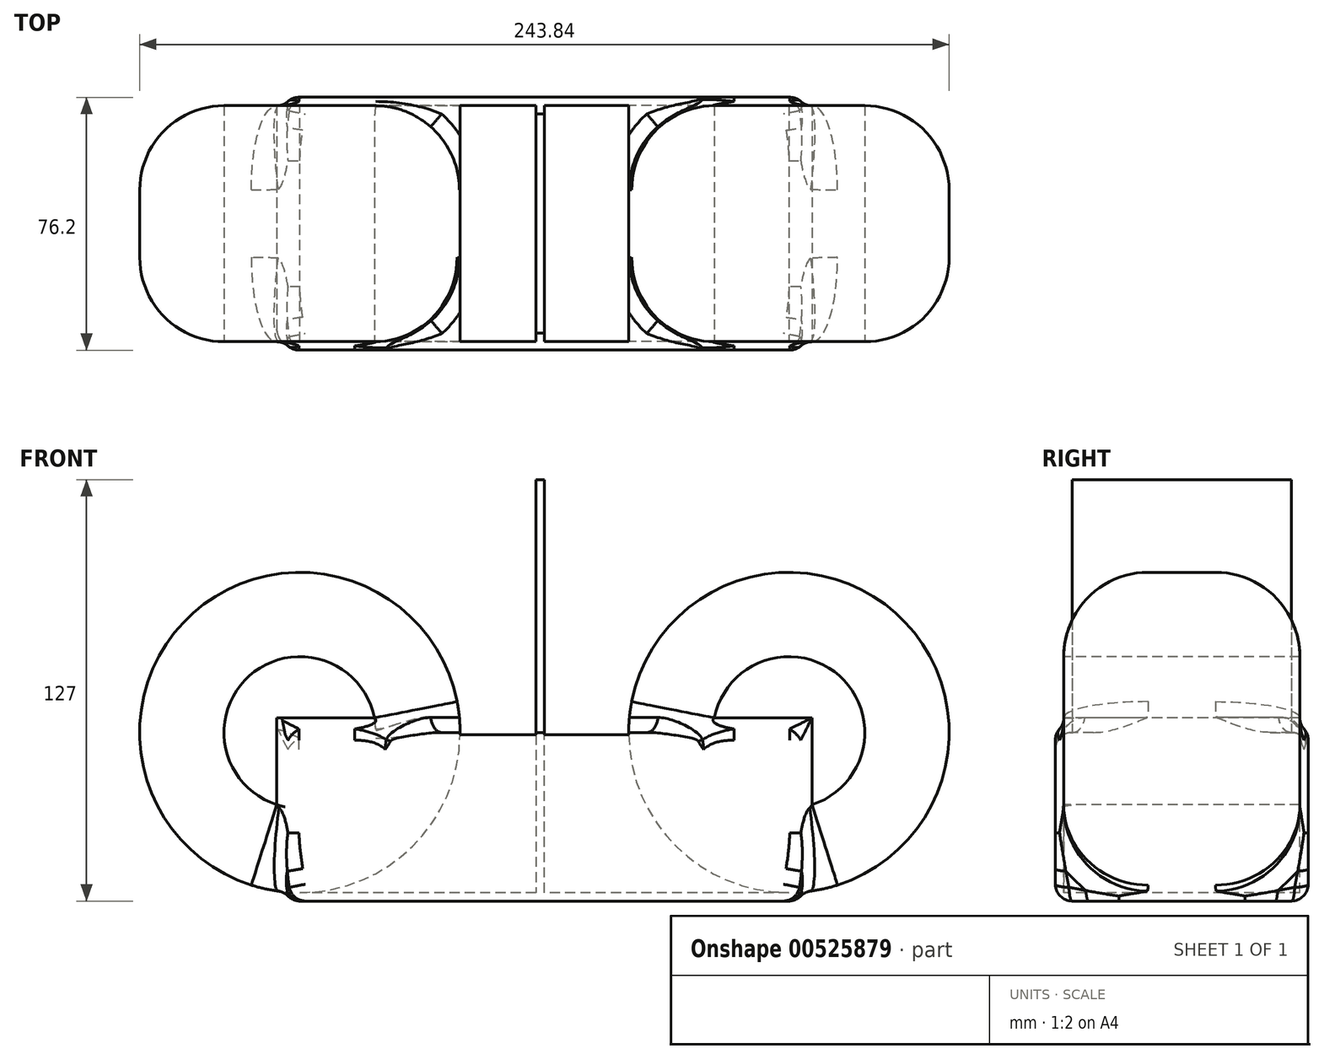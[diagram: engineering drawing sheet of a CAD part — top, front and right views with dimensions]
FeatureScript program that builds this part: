
annotation { "Feature Type Name" : "Feature", "Feature Type Description" : "" }
export const myFeature = defineFeature(function(context is Context, id is Id, definition is map)
    precondition{}
    {
        {
            var Q0;
            Q0=qCreatedBy(makeId("Top.planeOp"),FACE);
            var sketch = newSketch(context, id + "F0", { "sketchPlane" : qUnion([Q0])});
            skLineSegment(sketch, "E0.bottom", {"start": v(0, -43.56) * mm, "end": v(-76.2, -43.56) * mm});
            skLineSegment(sketch, "E0.top", {"start": v(0, 32.64) * mm, "end": v(-76.2, 32.64) * mm});
            skLineSegment(sketch, "E0.left", {"start": v(0, -43.56) * mm, "end": v(0, 32.64) * mm});
            skLineSegment(sketch, "E0.right", {"start": v(-76.2, -43.56) * mm, "end": v(-76.2, 32.64) * mm});
            skLineSegment(sketch, "E1.bottom", {"start": v(0, 32.64) * mm, "end": v(76.2, 32.64) * mm});
            skLineSegment(sketch, "E1.top", {"start": v(0, -43.56) * mm, "end": v(76.2, -43.56) * mm});
            skLineSegment(sketch, "E1.left", {"start": v(0, 32.64) * mm, "end": v(0, -43.56) * mm});
            skLineSegment(sketch, "E1.right", {"start": v(76.2, 32.64) * mm, "end": v(76.2, -43.56) * mm});
            skSolve(sketch);
        }
        {
            var Q0;
            Q0=makeQuery(id+"F0.imprint","IMPRINT",FACE,{"disambiguationData":[TD([[makeQuery(id+"F0.imprint","IMPRINT",EDGE,{"derivedFrom":sQuery(id+"F0.wireOp",EDGE,"E0.bottom")}),-1.0]])]});
            extrude(context, id + "F1", {"entities" : qUnion([Q0]), "depth" : 25.4 * mm, "offsetDistance" : 25.4 * mm});
        }
        {
            var Q0;
            Q0=makeQuery(id+"F1.opExtrude","CAP_FACE",FACE,{"disambiguationData":[OSD([sQuery(id+"F0.wireOp",EDGE,"E0.bottom"),sQuery(id+"F0.wireOp",EDGE,"E0.top"),sQuery(id+"F0.wireOp",EDGE,"E0.right"),sQuery(id+"F0.wireOp",EDGE,"E1.left")])],"isStart":false});
            shell(context, id + "F2", {"entities" : qUnion([Q0]), "thickness" : 2.54 * mm});
        }
        {
            var Q0;
            Q0=makeQuery(id+"F0.imprint","IMPRINT",FACE,{"disambiguationData":[TD([[makeQuery(id+"F0.imprint","IMPRINT",EDGE,{"derivedFrom":sQuery(id+"F0.wireOp",EDGE,"E1.bottom")}),-1.0]])]});
            extrude(context, id + "F3", {"entities" : qUnion([Q0]), "operationType" : NewBodyOperationType.ADD, "depth" : 25.4 * mm, "offsetDistance" : 25.4 * mm});
        }
        {
            var Q0;
            {var subQ0=sQuery(id+"F0.wireOp",EDGE,"E1.left");Q0=makeQuery(id+"F3.boolean.opBoolean","MERGE",FACE,{"derivedFrom":[makeQuery(id+"F1.opExtrude","CAP_FACE",FACE,{"disambiguationData":[OSD([sQuery(id+"F0.wireOp",EDGE,"E0.bottom"),sQuery(id+"F0.wireOp",EDGE,"E0.top"),sQuery(id+"F0.wireOp",EDGE,"E0.right"),subQ0])],"isStart":false}),makeQuery(id+"F3.opExtrude","CAP_FACE",FACE,{"disambiguationData":[OSD([sQuery(id+"F0.wireOp",EDGE,"E1.bottom"),sQuery(id+"F0.wireOp",EDGE,"E1.top"),subQ0,sQuery(id+"F0.wireOp",EDGE,"E1.right")])],"isStart":false})]});}
            shell(context, id + "F4", {"entities" : qUnion([Q0]), "thickness" : 2.54 * mm});
        }
        {
            var Q0;
            {var subQ0=sQuery(id+"F0.wireOp",EDGE,"E1.left");Q0=makeQuery(id+"F3.boolean.opBoolean","MERGE",FACE,{"derivedFrom":[makeQuery(id+"F1.opExtrude","CAP_FACE",FACE,{"disambiguationData":[OSD([sQuery(id+"F0.wireOp",EDGE,"E0.bottom"),sQuery(id+"F0.wireOp",EDGE,"E0.top"),sQuery(id+"F0.wireOp",EDGE,"E0.right"),subQ0])],"isStart":false}),makeQuery(id+"F3.opExtrude","CAP_FACE",FACE,{"disambiguationData":[OSD([sQuery(id+"F0.wireOp",EDGE,"E1.bottom"),sQuery(id+"F0.wireOp",EDGE,"E1.top"),subQ0,sQuery(id+"F0.wireOp",EDGE,"E1.right")])],"isStart":false})]});}
            extrude(context, id + "F5", {"entities" : qUnion([Q0]), "operationType" : NewBodyOperationType.ADD, "depth" : 25.4 * mm, "offsetDistance" : 25.4 * mm});
        }
        {
            var Q0;
            {var subQ0=sQuery(id+"F0.wireOp",EDGE,"E0.right");Q0=makeQuery(id+"F5.boolean.opBoolean","MERGE",FACE,{"derivedFrom":[makeQuery(id+"F2.opShell","OFFSET_FACE",FACE,{"disambiguationData":[OSD([subQ0])]}),makeQuery(id+"F5.opExtrude","SWEPT_FACE",FACE,{"disambiguationData":[OSD([subQ0]),TDD([makeQuery(id+"F2.opShell","OFFSET_EDGE",EDGE,{"disambiguationData":[OSD([subQ0]),TDD([makeQuery(id+"F1.opExtrude","CAP_EDGE",EDGE,{"disambiguationData":[OSD([subQ0])],"isStart":false})])]})])]})]});}
            var Q1;
            {var subQ0=sQuery(id+"F0.wireOp",EDGE,"E0.right");Q1=makeQuery(id+"F5.opExtrude","CAP_EDGE",EDGE,{"disambiguationData":[OSD([subQ0]),TDD([makeQuery(id+"F2.opShell","OFFSET_EDGE",EDGE,{"disambiguationData":[OSD([subQ0]),TDD([makeQuery(id+"F1.opExtrude","CAP_EDGE",EDGE,{"disambiguationData":[OSD([subQ0])],"isStart":false})])]})])],"isStart":false});}
            revolve(context, id + "F6", {"operationType" : NewBodyOperationType.ADD, "entities" : qUnion([Q0]), "axis" : qUnion([Q1]), "revolveType" : RevolveType.FULL});
        }
        {
            var Q0;
            {var subQ0=sQuery(id+"F0.wireOp",EDGE,"E1.right");Q0=makeQuery(id+"F5.boolean.opBoolean","MERGE",FACE,{"derivedFrom":[makeQuery(id+"F4.opShell","OFFSET_FACE",FACE,{"disambiguationData":[OSD([subQ0])]}),makeQuery(id+"F5.opExtrude","SWEPT_FACE",FACE,{"disambiguationData":[OSD([subQ0]),TDD([makeQuery(id+"F4.opShell","OFFSET_EDGE",EDGE,{"disambiguationData":[OSD([subQ0]),TDD([makeQuery(id+"F3.opExtrude","CAP_EDGE",EDGE,{"disambiguationData":[OSD([subQ0])],"isStart":false})])]})])]})]});}
            var Q1;
            {var subQ0=sQuery(id+"F0.wireOp",EDGE,"E1.right");Q1=makeQuery(id+"F5.opExtrude","CAP_EDGE",EDGE,{"disambiguationData":[OSD([subQ0]),TDD([makeQuery(id+"F4.opShell","OFFSET_EDGE",EDGE,{"disambiguationData":[OSD([subQ0]),TDD([makeQuery(id+"F3.opExtrude","CAP_EDGE",EDGE,{"disambiguationData":[OSD([subQ0])],"isStart":false})])]})])],"isStart":false});}
            revolve(context, id + "F7", {"operationType" : NewBodyOperationType.ADD, "entities" : qUnion([Q0]), "axis" : qUnion([Q1]), "revolveType" : RevolveType.FULL});
        }
        {
            var Q0;
            {var subQ0=sQuery(id+"F0.wireOp",EDGE,"E0.right");var subQ1=sQuery(id+"F0.wireOp",EDGE,"E0.bottom");Q0=makeQuery(id+"F6.boolean.opBoolean","INTERSECT",EDGE,{"derivedFrom":[makeQuery(id+"F5.opExtrude","CAP_FACE",FACE,{"disambiguationData":[OSD([subQ1,sQuery(id+"F0.wireOp",EDGE,"E0.top"),subQ0,sQuery(id+"F0.wireOp",EDGE,"E1.bottom"),sQuery(id+"F0.wireOp",EDGE,"E1.top"),sQuery(id+"F0.wireOp",EDGE,"E1.left"),sQuery(id+"F0.wireOp",EDGE,"E1.right")])],"isStart":false}),makeQuery(id+"F6.opRevolve","SWEPT_FACE",FACE,{"disambiguationData":[OSD([subQ1,subQ0])]})]});}
            var Q1;
            {var subQ0=sQuery(id+"F0.wireOp",EDGE,"E0.right");Q1=makeQuery(id+"F6.boolean.opBoolean","INTERSECT",EDGE,{"derivedFrom":[makeQuery(id+"F5.boolean.opBoolean","MERGE",FACE,{"derivedFrom":[makeQuery(id+"F1.opExtrude","SWEPT_FACE",FACE,{"disambiguationData":[OSD([subQ0])]}),makeQuery(id+"F5.opExtrude","SWEPT_FACE",FACE,{"disambiguationData":[OSD([subQ0]),TDD([makeQuery(id+"F1.opExtrude","CAP_EDGE",EDGE,{"disambiguationData":[OSD([subQ0])],"isStart":false})])]})]}),makeQuery(id+"F6.opRevolve","SWEPT_FACE",FACE,{"disambiguationData":[OSD([sQuery(id+"F0.wireOp",EDGE,"E0.bottom"),subQ0])]})]});}
            var Q2;
            {var subQ0=sQuery(id+"F0.wireOp",EDGE,"E0.right");Q2=makeQuery(id+"F6.boolean.opBoolean","INTERSECT",EDGE,{"derivedFrom":[makeQuery(id+"F5.boolean.opBoolean","MERGE",FACE,{"derivedFrom":[makeQuery(id+"F1.opExtrude","SWEPT_FACE",FACE,{"disambiguationData":[OSD([subQ0])]}),makeQuery(id+"F5.opExtrude","SWEPT_FACE",FACE,{"disambiguationData":[OSD([subQ0]),TDD([makeQuery(id+"F1.opExtrude","CAP_EDGE",EDGE,{"disambiguationData":[OSD([subQ0])],"isStart":false})])]})]}),makeQuery(id+"F6.opRevolve","SWEPT_FACE",FACE,{"disambiguationData":[OSD([subQ0])]})]});}
            var Q3;
            {var subQ0=sQuery(id+"F0.wireOp",EDGE,"E0.right");Q3=makeQuery(id+"F6.boolean.opBoolean","INTERSECT",EDGE,{"derivedFrom":[makeQuery(id+"F5.boolean.opBoolean","MERGE",FACE,{"derivedFrom":[makeQuery(id+"F1.opExtrude","SWEPT_FACE",FACE,{"disambiguationData":[OSD([subQ0])]}),makeQuery(id+"F5.opExtrude","SWEPT_FACE",FACE,{"disambiguationData":[OSD([subQ0]),TDD([makeQuery(id+"F1.opExtrude","CAP_EDGE",EDGE,{"disambiguationData":[OSD([subQ0])],"isStart":false})])]})]}),makeQuery(id+"F6.opRevolve","SWEPT_FACE",FACE,{"disambiguationData":[OSD([sQuery(id+"F0.wireOp",EDGE,"E0.top"),subQ0])]})]});}
            var Q4;
            {var subQ0=sQuery(id+"F0.wireOp",EDGE,"E1.right");Q4=makeQuery(id+"F7.boolean.opBoolean","INTERSECT",EDGE,{"derivedFrom":[makeQuery(id+"F5.boolean.opBoolean","MERGE",FACE,{"derivedFrom":[makeQuery(id+"F3.opExtrude","SWEPT_FACE",FACE,{"disambiguationData":[OSD([subQ0])]}),makeQuery(id+"F5.opExtrude","SWEPT_FACE",FACE,{"disambiguationData":[OSD([subQ0]),TDD([makeQuery(id+"F3.opExtrude","CAP_EDGE",EDGE,{"disambiguationData":[OSD([subQ0])],"isStart":false})])]})]}),makeQuery(id+"F7.opRevolve","SWEPT_FACE",FACE,{"disambiguationData":[OSD([sQuery(id+"F0.wireOp",EDGE,"E1.bottom"),subQ0])]})]});}
            var Q5;
            {var subQ0=sQuery(id+"F0.wireOp",EDGE,"E1.right");var subQ1=sQuery(id+"F0.wireOp",EDGE,"E1.bottom");Q5=makeQuery(id+"F7.boolean.opBoolean","INTERSECT",EDGE,{"derivedFrom":[makeQuery(id+"F5.opExtrude","CAP_FACE",FACE,{"disambiguationData":[OSD([sQuery(id+"F0.wireOp",EDGE,"E0.bottom"),sQuery(id+"F0.wireOp",EDGE,"E0.top"),sQuery(id+"F0.wireOp",EDGE,"E0.right"),subQ1,sQuery(id+"F0.wireOp",EDGE,"E1.top"),sQuery(id+"F0.wireOp",EDGE,"E1.left"),subQ0])],"isStart":false}),makeQuery(id+"F7.opRevolve","SWEPT_FACE",FACE,{"disambiguationData":[OSD([subQ1,subQ0])]})]});}
            var Q6;
            {var subQ0=sQuery(id+"F0.wireOp",EDGE,"E1.right");Q6=makeQuery(id+"F7.boolean.opBoolean","INTERSECT",EDGE,{"derivedFrom":[makeQuery(id+"F5.boolean.opBoolean","MERGE",FACE,{"derivedFrom":[makeQuery(id+"F3.opExtrude","SWEPT_FACE",FACE,{"disambiguationData":[OSD([subQ0])]}),makeQuery(id+"F5.opExtrude","SWEPT_FACE",FACE,{"disambiguationData":[OSD([subQ0]),TDD([makeQuery(id+"F3.opExtrude","CAP_EDGE",EDGE,{"disambiguationData":[OSD([subQ0])],"isStart":false})])]})]}),makeQuery(id+"F7.opRevolve","SWEPT_FACE",FACE,{"disambiguationData":[OSD([sQuery(id+"F0.wireOp",EDGE,"E1.top"),subQ0])]})]});}
            var Q7;
            {var subQ0=sQuery(id+"F0.wireOp",EDGE,"E1.right");Q7=makeQuery(id+"F7.boolean.opBoolean","INTERSECT",EDGE,{"derivedFrom":[makeQuery(id+"F5.boolean.opBoolean","MERGE",FACE,{"derivedFrom":[makeQuery(id+"F3.opExtrude","SWEPT_FACE",FACE,{"disambiguationData":[OSD([subQ0])]}),makeQuery(id+"F5.opExtrude","SWEPT_FACE",FACE,{"disambiguationData":[OSD([subQ0]),TDD([makeQuery(id+"F3.opExtrude","CAP_EDGE",EDGE,{"disambiguationData":[OSD([subQ0])],"isStart":false})])]})]}),makeQuery(id+"F7.opRevolve","SWEPT_FACE",FACE,{"disambiguationData":[OSD([subQ0])]})]});}
            var Q8;
            {var subQ0=sQuery(id+"F0.wireOp",EDGE,"E1.right");var subQ1=sQuery(id+"F0.wireOp",EDGE,"E1.top");Q8=makeQuery(id+"F7.boolean.opBoolean","INTERSECT",EDGE,{"derivedFrom":[makeQuery(id+"F5.opExtrude","CAP_FACE",FACE,{"disambiguationData":[OSD([sQuery(id+"F0.wireOp",EDGE,"E0.bottom"),sQuery(id+"F0.wireOp",EDGE,"E0.top"),sQuery(id+"F0.wireOp",EDGE,"E0.right"),sQuery(id+"F0.wireOp",EDGE,"E1.bottom"),subQ1,sQuery(id+"F0.wireOp",EDGE,"E1.left"),subQ0])],"isStart":false}),makeQuery(id+"F7.opRevolve","SWEPT_FACE",FACE,{"disambiguationData":[OSD([subQ1,subQ0])]})]});}
            fillet(context, id + "F8", {"entities" : qUnion([Q0, Q1, Q2, Q3, Q4, Q5, Q6, Q7, Q8]), "radius" : 5.08 * mm, "tangentPropagation" : true, "allowEdgeOverflow" : false});
        }
        {
            var Q0;
            Q0=makeQuery(id+"F3.boolean.opBoolean","MERGE",EDGE,{"derivedFrom":[makeQuery(id+"F1.opExtrude","CAP_EDGE",EDGE,{"disambiguationData":[OSD([sQuery(id+"F0.wireOp",EDGE,"E0.bottom")])],"isStart":true}),makeQuery(id+"F3.opExtrude","CAP_EDGE",EDGE,{"disambiguationData":[OSD([sQuery(id+"F0.wireOp",EDGE,"E1.top")])],"isStart":true})]});
            var Q1;
            Q1=makeQuery(id+"F3.boolean.opBoolean","MERGE",EDGE,{"derivedFrom":[makeQuery(id+"F1.opExtrude","CAP_EDGE",EDGE,{"disambiguationData":[OSD([sQuery(id+"F0.wireOp",EDGE,"E0.top")])],"isStart":true}),makeQuery(id+"F3.opExtrude","CAP_EDGE",EDGE,{"disambiguationData":[OSD([sQuery(id+"F0.wireOp",EDGE,"E1.bottom")])],"isStart":true})]});
            fillet(context, id + "F9", {"entities" : qUnion([Q0, Q1]), "radius" : 5.08 * mm, "tangentPropagation" : true, "allowEdgeOverflow" : false});
        }
        {
            var Q0;
            {var subQ0=sQuery(id+"F0.wireOp",EDGE,"E1.right");var subQ1=sQuery(id+"F0.wireOp",EDGE,"E1.top");Q0=makeQuery(id+"F7.boolean.opBoolean","SPLIT",EDGE,{"disambiguationData":[topologyDisambiguationEdgeConnected([makeQuery(id+"F7.opRevolve","SWEPT_FACE",FACE,{"disambiguationData":[OSD([subQ1,subQ0])]})])],"derivedFrom":makeQuery(id+"F7.opRevolve","SWEPT_EDGE",EDGE,{"disambiguationData":[OSD([subQ1,subQ0])]})});}
            var Q1;
            {var subQ0=sQuery(id+"F0.wireOp",EDGE,"E1.right");var subQ1=sQuery(id+"F0.wireOp",EDGE,"E1.bottom");Q1=makeQuery(id+"F7.boolean.opBoolean","SPLIT",EDGE,{"disambiguationData":[topologyDisambiguationEdgeConnected([makeQuery(id+"F7.opRevolve","SWEPT_FACE",FACE,{"disambiguationData":[OSD([subQ1,subQ0])]})])],"derivedFrom":makeQuery(id+"F7.opRevolve","SWEPT_EDGE",EDGE,{"disambiguationData":[OSD([subQ1,subQ0])]})});}
            var Q2;
            {var subQ0=sQuery(id+"F0.wireOp",EDGE,"E0.right");var subQ1=sQuery(id+"F0.wireOp",EDGE,"E0.top");Q2=makeQuery(id+"F6.boolean.opBoolean","SPLIT",EDGE,{"disambiguationData":[topologyDisambiguationEdgeConnected([makeQuery(id+"F6.opRevolve","SWEPT_FACE",FACE,{"disambiguationData":[OSD([subQ1,subQ0])]})])],"derivedFrom":makeQuery(id+"F6.opRevolve","SWEPT_EDGE",EDGE,{"disambiguationData":[OSD([subQ1,subQ0])]})});}
            var Q3;
            {var subQ0=sQuery(id+"F0.wireOp",EDGE,"E0.right");var subQ1=sQuery(id+"F0.wireOp",EDGE,"E0.bottom");Q3=makeQuery(id+"F6.boolean.opBoolean","SPLIT",EDGE,{"disambiguationData":[topologyDisambiguationEdgeConnected([makeQuery(id+"F6.opRevolve","SWEPT_FACE",FACE,{"disambiguationData":[OSD([subQ1,subQ0])]})])],"derivedFrom":makeQuery(id+"F6.opRevolve","SWEPT_EDGE",EDGE,{"disambiguationData":[OSD([subQ1,subQ0])]})});}
            fillet(context, id + "F10", {"entities" : qUnion([Q0, Q1, Q2, Q3]), "radius" : 25.4 * mm, "tangentPropagation" : true, "allowEdgeOverflow" : false});
        }
        {
            var Q0;
            {var subQ0=sQuery(id+"F0.wireOp",EDGE,"E1.top");var subQ1=sQuery(id+"F0.wireOp",EDGE,"E0.bottom");var subQ2=makeQuery(id+"F3.boolean.opBoolean","MERGE",EDGE,{"derivedFrom":[makeQuery(id+"F1.opExtrude","CAP_EDGE",EDGE,{"disambiguationData":[OSD([subQ1])],"isStart":false}),makeQuery(id+"F3.opExtrude","CAP_EDGE",EDGE,{"disambiguationData":[OSD([subQ0])],"isStart":false})]});var subQ3=makeQuery(id+"F5.boolean.opBoolean","MERGE",FACE,{"derivedFrom":[makeQuery(id+"F3.boolean.opBoolean","MERGE",FACE,{"derivedFrom":[makeQuery(id+"F1.opExtrude","SWEPT_FACE",FACE,{"disambiguationData":[OSD([subQ1])]}),makeQuery(id+"F3.opExtrude","SWEPT_FACE",FACE,{"disambiguationData":[OSD([subQ0])]})]}),makeQuery(id+"F5.opExtrude","SWEPT_FACE",FACE,{"disambiguationData":[OSD([subQ1,subQ0]),TDD([subQ2])]})]});var subQ4=sQuery(id+"F0.wireOp",EDGE,"E1.right");var subQ5=sQuery(id+"F0.wireOp",EDGE,"E0.right");var subQ6=makeQuery(id+"F5.opExtrude","CAP_FACE",FACE,{"disambiguationData":[OSD([subQ1,sQuery(id+"F0.wireOp",EDGE,"E0.top"),subQ5,sQuery(id+"F0.wireOp",EDGE,"E1.bottom"),subQ0,sQuery(id+"F0.wireOp",EDGE,"E1.left"),subQ4])],"isStart":false});Q0=makeQuery(id+"F10.opFillet","MERGE",EDGE,{"derivedFrom":[makeQuery(id+"F5.opExtrude","CAP_EDGE",EDGE,{"disambiguationData":[OSD([subQ1,subQ0]),TDD([subQ2])],"isStart":false}),makeQuery(id+"F8.opFillet","BLEND_EDGE",EDGE,{"blendedFrom":[makeQuery(id+"F6.boolean.opBoolean","INTERSECT",EDGE,{"derivedFrom":[subQ6,makeQuery(id+"F6.opRevolve","SWEPT_FACE",FACE,{"disambiguationData":[OSD([subQ1,subQ5])]})]}),subQ3],"blendedInto":[subQ3]}),makeQuery(id+"F8.opFillet","BLEND_EDGE",EDGE,{"blendedFrom":[makeQuery(id+"F7.boolean.opBoolean","INTERSECT",EDGE,{"derivedFrom":[subQ6,makeQuery(id+"F7.opRevolve","SWEPT_FACE",FACE,{"disambiguationData":[OSD([subQ0,subQ4])]})]}),subQ3],"blendedInto":[subQ3]})]});}
            var Q1;
            {var subQ0=sQuery(id+"F0.wireOp",EDGE,"E1.bottom");var subQ1=sQuery(id+"F0.wireOp",EDGE,"E0.top");var subQ2=makeQuery(id+"F3.boolean.opBoolean","MERGE",EDGE,{"derivedFrom":[makeQuery(id+"F1.opExtrude","CAP_EDGE",EDGE,{"disambiguationData":[OSD([subQ1])],"isStart":false}),makeQuery(id+"F3.opExtrude","CAP_EDGE",EDGE,{"disambiguationData":[OSD([subQ0])],"isStart":false})]});var subQ3=sQuery(id+"F0.wireOp",EDGE,"E1.right");Q1=makeQuery(id+"F10.opFillet","MERGE",EDGE,{"derivedFrom":[makeQuery(id+"F5.opExtrude","CAP_EDGE",EDGE,{"disambiguationData":[OSD([subQ1,subQ0]),TDD([subQ2])],"isStart":false}),makeQuery(id+"F8.opFillet","BLEND_EDGE",EDGE,{"blendedFrom":[makeQuery(id+"F7.boolean.opBoolean","INTERSECT",EDGE,{"derivedFrom":[makeQuery(id+"F5.opExtrude","CAP_FACE",FACE,{"disambiguationData":[OSD([sQuery(id+"F0.wireOp",EDGE,"E0.bottom"),subQ1,sQuery(id+"F0.wireOp",EDGE,"E0.right"),subQ0,sQuery(id+"F0.wireOp",EDGE,"E1.top"),sQuery(id+"F0.wireOp",EDGE,"E1.left"),subQ3])],"isStart":false}),makeQuery(id+"F7.opRevolve","SWEPT_FACE",FACE,{"disambiguationData":[OSD([subQ0,subQ3])]})]}),makeQuery(id+"F5.boolean.opBoolean","MERGE",FACE,{"derivedFrom":[makeQuery(id+"F3.boolean.opBoolean","MERGE",FACE,{"derivedFrom":[makeQuery(id+"F1.opExtrude","SWEPT_FACE",FACE,{"disambiguationData":[OSD([subQ1])]}),makeQuery(id+"F3.opExtrude","SWEPT_FACE",FACE,{"disambiguationData":[OSD([subQ0])]})]}),makeQuery(id+"F5.opExtrude","SWEPT_FACE",FACE,{"disambiguationData":[OSD([subQ1,subQ0]),TDD([subQ2])]})]})],"blendedInto":[makeQuery(id+"F5.boolean.opBoolean","MERGE",FACE,{"derivedFrom":[makeQuery(id+"F3.boolean.opBoolean","MERGE",FACE,{"derivedFrom":[makeQuery(id+"F1.opExtrude","SWEPT_FACE",FACE,{"disambiguationData":[OSD([subQ1])]}),makeQuery(id+"F3.opExtrude","SWEPT_FACE",FACE,{"disambiguationData":[OSD([subQ0])]})]}),makeQuery(id+"F5.opExtrude","SWEPT_FACE",FACE,{"disambiguationData":[OSD([subQ1,subQ0]),TDD([subQ2])]})]})]})]});}
            fillet(context, id + "F11", {"entities" : qUnion([Q0, Q1]), "radius" : 5.08 * mm, "tangentPropagation" : true, "allowEdgeOverflow" : false});
        }
        {
            var Q0;
            {var subQ0=sQuery(id+"F0.wireOp",EDGE,"E0.right");var subQ1=sQuery(id+"F0.wireOp",EDGE,"E0.top");var subQ2=sQuery(id+"F0.wireOp",EDGE,"E1.bottom");var subQ3=makeQuery(id+"F3.boolean.opBoolean","MERGE",EDGE,{"derivedFrom":[makeQuery(id+"F1.opExtrude","CAP_EDGE",EDGE,{"disambiguationData":[OSD([subQ1])],"isStart":false}),makeQuery(id+"F3.opExtrude","CAP_EDGE",EDGE,{"disambiguationData":[OSD([subQ2])],"isStart":false})]});var subQ4=sQuery(id+"F0.wireOp",EDGE,"E1.right");Q0=makeQuery(id+"F11.opFillet","BLEND_EDGE",EDGE,{"blendedFrom":[makeQuery(id+"F10.opFillet","MERGE",EDGE,{"derivedFrom":[makeQuery(id+"F5.opExtrude","CAP_EDGE",EDGE,{"disambiguationData":[OSD([subQ1,subQ2]),TDD([subQ3])],"isStart":false}),makeQuery(id+"F8.opFillet","BLEND_EDGE",EDGE,{"blendedFrom":[makeQuery(id+"F7.boolean.opBoolean","INTERSECT",EDGE,{"derivedFrom":[makeQuery(id+"F5.opExtrude","CAP_FACE",FACE,{"disambiguationData":[OSD([sQuery(id+"F0.wireOp",EDGE,"E0.bottom"),subQ1,subQ0,subQ2,sQuery(id+"F0.wireOp",EDGE,"E1.top"),sQuery(id+"F0.wireOp",EDGE,"E1.left"),subQ4])],"isStart":false}),makeQuery(id+"F7.opRevolve","SWEPT_FACE",FACE,{"disambiguationData":[OSD([subQ2,subQ4])]})]}),makeQuery(id+"F5.boolean.opBoolean","MERGE",FACE,{"derivedFrom":[makeQuery(id+"F3.boolean.opBoolean","MERGE",FACE,{"derivedFrom":[makeQuery(id+"F1.opExtrude","SWEPT_FACE",FACE,{"disambiguationData":[OSD([subQ1])]}),makeQuery(id+"F3.opExtrude","SWEPT_FACE",FACE,{"disambiguationData":[OSD([subQ2])]})]}),makeQuery(id+"F5.opExtrude","SWEPT_FACE",FACE,{"disambiguationData":[OSD([subQ1,subQ2]),TDD([subQ3])]})]})],"blendedInto":[makeQuery(id+"F5.boolean.opBoolean","MERGE",FACE,{"derivedFrom":[makeQuery(id+"F3.boolean.opBoolean","MERGE",FACE,{"derivedFrom":[makeQuery(id+"F1.opExtrude","SWEPT_FACE",FACE,{"disambiguationData":[OSD([subQ1])]}),makeQuery(id+"F3.opExtrude","SWEPT_FACE",FACE,{"disambiguationData":[OSD([subQ2])]})]}),makeQuery(id+"F5.opExtrude","SWEPT_FACE",FACE,{"disambiguationData":[OSD([subQ1,subQ2]),TDD([subQ3])]})]})]})]}),makeQuery(id+"F6.opRevolve","SWEPT_FACE",FACE,{"disambiguationData":[OSD([subQ1,subQ0])]})],"blendedInto":[makeQuery(id+"F6.opRevolve","SWEPT_FACE",FACE,{"disambiguationData":[OSD([subQ1,subQ0])]})]});}
            var Q1;
            {var subQ0=sQuery(id+"F0.wireOp",EDGE,"E1.right");var subQ1=sQuery(id+"F0.wireOp",EDGE,"E1.bottom");var subQ2=sQuery(id+"F0.wireOp",EDGE,"E1.left");var subQ3=sQuery(id+"F0.wireOp",EDGE,"E1.top");var subQ4=sQuery(id+"F0.wireOp",EDGE,"E0.right");var subQ5=sQuery(id+"F0.wireOp",EDGE,"E0.top");var subQ6=sQuery(id+"F0.wireOp",EDGE,"E0.bottom");var subQ7=makeQuery(id+"F7.boolean.opBoolean","INTERSECT",EDGE,{"derivedFrom":[makeQuery(id+"F5.opExtrude","CAP_FACE",FACE,{"disambiguationData":[OSD([subQ6,subQ5,subQ4,subQ1,subQ3,subQ2,subQ0])],"isStart":false}),makeQuery(id+"F7.opRevolve","SWEPT_FACE",FACE,{"disambiguationData":[OSD([subQ1,subQ0])]})]});var subQ8=makeQuery(id+"F3.boolean.opBoolean","MERGE",EDGE,{"derivedFrom":[makeQuery(id+"F1.opExtrude","CAP_EDGE",EDGE,{"disambiguationData":[OSD([subQ5])],"isStart":false}),makeQuery(id+"F3.opExtrude","CAP_EDGE",EDGE,{"disambiguationData":[OSD([subQ1])],"isStart":false})]});Q1=makeQuery(id+"F11.opFillet","BLEND_EDGE",EDGE,{"blendedFrom":[makeQuery(id+"F10.opFillet","MERGE",EDGE,{"derivedFrom":[makeQuery(id+"F5.opExtrude","CAP_EDGE",EDGE,{"disambiguationData":[OSD([subQ5,subQ1]),TDD([subQ8])],"isStart":false}),makeQuery(id+"F8.opFillet","BLEND_EDGE",EDGE,{"blendedFrom":[subQ7,makeQuery(id+"F5.boolean.opBoolean","MERGE",FACE,{"derivedFrom":[makeQuery(id+"F3.boolean.opBoolean","MERGE",FACE,{"derivedFrom":[makeQuery(id+"F1.opExtrude","SWEPT_FACE",FACE,{"disambiguationData":[OSD([subQ5])]}),makeQuery(id+"F3.opExtrude","SWEPT_FACE",FACE,{"disambiguationData":[OSD([subQ1])]})]}),makeQuery(id+"F5.opExtrude","SWEPT_FACE",FACE,{"disambiguationData":[OSD([subQ5,subQ1]),TDD([subQ8])]})]})],"blendedInto":[makeQuery(id+"F5.boolean.opBoolean","MERGE",FACE,{"derivedFrom":[makeQuery(id+"F3.boolean.opBoolean","MERGE",FACE,{"derivedFrom":[makeQuery(id+"F1.opExtrude","SWEPT_FACE",FACE,{"disambiguationData":[OSD([subQ5])]}),makeQuery(id+"F3.opExtrude","SWEPT_FACE",FACE,{"disambiguationData":[OSD([subQ1])]})]}),makeQuery(id+"F5.opExtrude","SWEPT_FACE",FACE,{"disambiguationData":[OSD([subQ5,subQ1]),TDD([subQ8])]})]})]})]}),makeQuery(id+"F10.opFillet","BLEND_FACE",FACE,{"disambiguationData":[OSD([subQ6,subQ5,subQ4,subQ1,subQ3,subQ2,subQ0]),TDD([makeQuery(id+"F8.opFillet","BLEND_EDGE",EDGE,{"blendedFrom":[subQ7,makeQuery(id+"F7.opRevolve","SWEPT_FACE",FACE,{"disambiguationData":[OSD([subQ0])]})],"blendedInto":[makeQuery(id+"F7.opRevolve","SWEPT_FACE",FACE,{"disambiguationData":[OSD([subQ0])]})]})])]})],"blendedInto":[makeQuery(id+"F10.opFillet","BLEND_FACE",FACE,{"disambiguationData":[OSD([subQ6,subQ5,subQ4,subQ1,subQ3,subQ2,subQ0]),TDD([makeQuery(id+"F8.opFillet","BLEND_EDGE",EDGE,{"blendedFrom":[subQ7,makeQuery(id+"F7.opRevolve","SWEPT_FACE",FACE,{"disambiguationData":[OSD([subQ0])]})],"blendedInto":[makeQuery(id+"F7.opRevolve","SWEPT_FACE",FACE,{"disambiguationData":[OSD([subQ0])]})]})])]})]});}
            var Q2;
            {var subQ0=sQuery(id+"F0.wireOp",EDGE,"E0.right");var subQ1=sQuery(id+"F0.wireOp",EDGE,"E0.bottom");var subQ2=sQuery(id+"F0.wireOp",EDGE,"E1.right");var subQ3=sQuery(id+"F0.wireOp",EDGE,"E1.left");var subQ4=sQuery(id+"F0.wireOp",EDGE,"E1.top");var subQ5=sQuery(id+"F0.wireOp",EDGE,"E1.bottom");var subQ6=sQuery(id+"F0.wireOp",EDGE,"E0.top");var subQ7=makeQuery(id+"F5.opExtrude","CAP_FACE",FACE,{"disambiguationData":[OSD([subQ1,subQ6,subQ0,subQ5,subQ4,subQ3,subQ2])],"isStart":false});var subQ8=makeQuery(id+"F6.boolean.opBoolean","INTERSECT",EDGE,{"derivedFrom":[subQ7,makeQuery(id+"F6.opRevolve","SWEPT_FACE",FACE,{"disambiguationData":[OSD([subQ1,subQ0])]})]});var subQ9=makeQuery(id+"F3.boolean.opBoolean","MERGE",EDGE,{"derivedFrom":[makeQuery(id+"F1.opExtrude","CAP_EDGE",EDGE,{"disambiguationData":[OSD([subQ1])],"isStart":false}),makeQuery(id+"F3.opExtrude","CAP_EDGE",EDGE,{"disambiguationData":[OSD([subQ4])],"isStart":false})]});var subQ10=makeQuery(id+"F5.boolean.opBoolean","MERGE",FACE,{"derivedFrom":[makeQuery(id+"F3.boolean.opBoolean","MERGE",FACE,{"derivedFrom":[makeQuery(id+"F1.opExtrude","SWEPT_FACE",FACE,{"disambiguationData":[OSD([subQ1])]}),makeQuery(id+"F3.opExtrude","SWEPT_FACE",FACE,{"disambiguationData":[OSD([subQ4])]})]}),makeQuery(id+"F5.opExtrude","SWEPT_FACE",FACE,{"disambiguationData":[OSD([subQ1,subQ4]),TDD([subQ9])]})]});Q2=makeQuery(id+"F11.opFillet","BLEND_EDGE",EDGE,{"blendedFrom":[makeQuery(id+"F10.opFillet","MERGE",EDGE,{"derivedFrom":[makeQuery(id+"F5.opExtrude","CAP_EDGE",EDGE,{"disambiguationData":[OSD([subQ1,subQ4]),TDD([subQ9])],"isStart":false}),makeQuery(id+"F8.opFillet","BLEND_EDGE",EDGE,{"blendedFrom":[subQ8,subQ10],"blendedInto":[subQ10]}),makeQuery(id+"F8.opFillet","BLEND_EDGE",EDGE,{"blendedFrom":[makeQuery(id+"F7.boolean.opBoolean","INTERSECT",EDGE,{"derivedFrom":[subQ7,makeQuery(id+"F7.opRevolve","SWEPT_FACE",FACE,{"disambiguationData":[OSD([subQ4,subQ2])]})]}),subQ10],"blendedInto":[subQ10]})]}),makeQuery(id+"F10.opFillet","BLEND_FACE",FACE,{"disambiguationData":[OSD([subQ1,subQ6,subQ0,subQ5,subQ4,subQ3,subQ2]),TDD([makeQuery(id+"F8.opFillet","BLEND_EDGE",EDGE,{"blendedFrom":[subQ8,makeQuery(id+"F6.opRevolve","SWEPT_FACE",FACE,{"disambiguationData":[OSD([subQ0])]})],"blendedInto":[makeQuery(id+"F6.opRevolve","SWEPT_FACE",FACE,{"disambiguationData":[OSD([subQ0])]})]})])]})],"blendedInto":[makeQuery(id+"F10.opFillet","BLEND_FACE",FACE,{"disambiguationData":[OSD([subQ1,subQ6,subQ0,subQ5,subQ4,subQ3,subQ2]),TDD([makeQuery(id+"F8.opFillet","BLEND_EDGE",EDGE,{"blendedFrom":[subQ8,makeQuery(id+"F6.opRevolve","SWEPT_FACE",FACE,{"disambiguationData":[OSD([subQ0])]})],"blendedInto":[makeQuery(id+"F6.opRevolve","SWEPT_FACE",FACE,{"disambiguationData":[OSD([subQ0])]})]})])]})]});}
            var Q3;
            {var subQ0=sQuery(id+"F0.wireOp",EDGE,"E1.right");var subQ1=sQuery(id+"F0.wireOp",EDGE,"E1.top");var subQ2=sQuery(id+"F0.wireOp",EDGE,"E1.left");var subQ3=sQuery(id+"F0.wireOp",EDGE,"E1.bottom");var subQ4=sQuery(id+"F0.wireOp",EDGE,"E0.right");var subQ5=sQuery(id+"F0.wireOp",EDGE,"E0.top");var subQ6=sQuery(id+"F0.wireOp",EDGE,"E0.bottom");var subQ7=makeQuery(id+"F5.opExtrude","CAP_FACE",FACE,{"disambiguationData":[OSD([subQ6,subQ5,subQ4,subQ3,subQ1,subQ2,subQ0])],"isStart":false});var subQ8=makeQuery(id+"F7.boolean.opBoolean","INTERSECT",EDGE,{"derivedFrom":[subQ7,makeQuery(id+"F7.opRevolve","SWEPT_FACE",FACE,{"disambiguationData":[OSD([subQ1,subQ0])]})]});var subQ9=makeQuery(id+"F3.boolean.opBoolean","MERGE",EDGE,{"derivedFrom":[makeQuery(id+"F1.opExtrude","CAP_EDGE",EDGE,{"disambiguationData":[OSD([subQ6])],"isStart":false}),makeQuery(id+"F3.opExtrude","CAP_EDGE",EDGE,{"disambiguationData":[OSD([subQ1])],"isStart":false})]});var subQ10=makeQuery(id+"F5.boolean.opBoolean","MERGE",FACE,{"derivedFrom":[makeQuery(id+"F3.boolean.opBoolean","MERGE",FACE,{"derivedFrom":[makeQuery(id+"F1.opExtrude","SWEPT_FACE",FACE,{"disambiguationData":[OSD([subQ6])]}),makeQuery(id+"F3.opExtrude","SWEPT_FACE",FACE,{"disambiguationData":[OSD([subQ1])]})]}),makeQuery(id+"F5.opExtrude","SWEPT_FACE",FACE,{"disambiguationData":[OSD([subQ6,subQ1]),TDD([subQ9])]})]});Q3=makeQuery(id+"F11.opFillet","BLEND_EDGE",EDGE,{"blendedFrom":[makeQuery(id+"F10.opFillet","MERGE",EDGE,{"derivedFrom":[makeQuery(id+"F5.opExtrude","CAP_EDGE",EDGE,{"disambiguationData":[OSD([subQ6,subQ1]),TDD([subQ9])],"isStart":false}),makeQuery(id+"F8.opFillet","BLEND_EDGE",EDGE,{"blendedFrom":[makeQuery(id+"F6.boolean.opBoolean","INTERSECT",EDGE,{"derivedFrom":[subQ7,makeQuery(id+"F6.opRevolve","SWEPT_FACE",FACE,{"disambiguationData":[OSD([subQ6,subQ4])]})]}),subQ10],"blendedInto":[subQ10]}),makeQuery(id+"F8.opFillet","BLEND_EDGE",EDGE,{"blendedFrom":[subQ8,subQ10],"blendedInto":[subQ10]})]}),makeQuery(id+"F10.opFillet","BLEND_FACE",FACE,{"disambiguationData":[OSD([subQ6,subQ5,subQ4,subQ3,subQ1,subQ2,subQ0]),TDD([makeQuery(id+"F8.opFillet","BLEND_EDGE",EDGE,{"blendedFrom":[subQ8,makeQuery(id+"F7.opRevolve","SWEPT_FACE",FACE,{"disambiguationData":[OSD([subQ0])]})],"blendedInto":[makeQuery(id+"F7.opRevolve","SWEPT_FACE",FACE,{"disambiguationData":[OSD([subQ0])]})]})])]})],"blendedInto":[makeQuery(id+"F10.opFillet","BLEND_FACE",FACE,{"disambiguationData":[OSD([subQ6,subQ5,subQ4,subQ3,subQ1,subQ2,subQ0]),TDD([makeQuery(id+"F8.opFillet","BLEND_EDGE",EDGE,{"blendedFrom":[subQ8,makeQuery(id+"F7.opRevolve","SWEPT_FACE",FACE,{"disambiguationData":[OSD([subQ0])]})],"blendedInto":[makeQuery(id+"F7.opRevolve","SWEPT_FACE",FACE,{"disambiguationData":[OSD([subQ0])]})]})])]})]});}
            fillet(context, id + "F12", {"entities" : qUnion([Q0, Q1, Q2, Q3]), "radius" : 5.08 * mm, "tangentPropagation" : true, "allowEdgeOverflow" : false});
        }
        {
            var Q0;
            Q0=makeQuery(id+"F11.opFillet","SPLIT",FACE,{"disambiguationData":[OD(4.0)],"derivedFrom":makeQuery(id+"F5.opExtrude","CAP_FACE",FACE,{"disambiguationData":[OSD([sQuery(id+"F0.wireOp",EDGE,"E0.bottom"),sQuery(id+"F0.wireOp",EDGE,"E0.top"),sQuery(id+"F0.wireOp",EDGE,"E0.right"),sQuery(id+"F0.wireOp",EDGE,"E1.bottom"),sQuery(id+"F0.wireOp",EDGE,"E1.top"),sQuery(id+"F0.wireOp",EDGE,"E1.left"),sQuery(id+"F0.wireOp",EDGE,"E1.right")])],"isStart":false})});
            extrude(context, id + "F13", {"entities" : qUnion([Q0]), "operationType" : NewBodyOperationType.ADD, "depth" : 76.2 * mm, "offsetDistance" : 25.4 * mm});
        }
        {
            var Q0;
            {var subQ0=sQuery(id+"F0.wireOp",EDGE,"E1.left");var subQ1=sQuery(id+"F0.wireOp",EDGE,"E0.right");Q0=makeQuery(id+"F8.opFillet","BLEND_EDGE",EDGE,{"blendedFrom":[makeQuery(id+"F6.boolean.opBoolean","INTERSECT",EDGE,{"derivedFrom":[makeQuery(id+"F5.boolean.opBoolean","MERGE",FACE,{"derivedFrom":[makeQuery(id+"F1.opExtrude","SWEPT_FACE",FACE,{"disambiguationData":[OSD([subQ1])]}),makeQuery(id+"F5.opExtrude","SWEPT_FACE",FACE,{"disambiguationData":[OSD([subQ1]),TDD([makeQuery(id+"F1.opExtrude","CAP_EDGE",EDGE,{"disambiguationData":[OSD([subQ1])],"isStart":false})])]})]}),makeQuery(id+"F6.opRevolve","SWEPT_FACE",FACE,{"disambiguationData":[OSD([subQ1])]})]}),makeQuery(id+"F3.boolean.opBoolean","MERGE",FACE,{"derivedFrom":[makeQuery(id+"F1.opExtrude","CAP_FACE",FACE,{"disambiguationData":[OSD([sQuery(id+"F0.wireOp",EDGE,"E0.bottom"),sQuery(id+"F0.wireOp",EDGE,"E0.top"),subQ1,subQ0])],"isStart":true}),makeQuery(id+"F3.opExtrude","CAP_FACE",FACE,{"disambiguationData":[OSD([sQuery(id+"F0.wireOp",EDGE,"E1.bottom"),sQuery(id+"F0.wireOp",EDGE,"E1.top"),subQ0,sQuery(id+"F0.wireOp",EDGE,"E1.right")])],"isStart":true})]})],"blendedInto":[makeQuery(id+"F3.boolean.opBoolean","MERGE",FACE,{"derivedFrom":[makeQuery(id+"F1.opExtrude","CAP_FACE",FACE,{"disambiguationData":[OSD([sQuery(id+"F0.wireOp",EDGE,"E0.bottom"),sQuery(id+"F0.wireOp",EDGE,"E0.top"),subQ1,subQ0])],"isStart":true}),makeQuery(id+"F3.opExtrude","CAP_FACE",FACE,{"disambiguationData":[OSD([sQuery(id+"F0.wireOp",EDGE,"E1.bottom"),sQuery(id+"F0.wireOp",EDGE,"E1.top"),subQ0,sQuery(id+"F0.wireOp",EDGE,"E1.right")])],"isStart":true})]})]});}
            var Q1;
            {var subQ0=sQuery(id+"F0.wireOp",EDGE,"E1.right");var subQ1=sQuery(id+"F0.wireOp",EDGE,"E1.left");Q1=makeQuery(id+"F8.opFillet","BLEND_EDGE",EDGE,{"blendedFrom":[makeQuery(id+"F7.boolean.opBoolean","INTERSECT",EDGE,{"derivedFrom":[makeQuery(id+"F5.boolean.opBoolean","MERGE",FACE,{"derivedFrom":[makeQuery(id+"F3.opExtrude","SWEPT_FACE",FACE,{"disambiguationData":[OSD([subQ0])]}),makeQuery(id+"F5.opExtrude","SWEPT_FACE",FACE,{"disambiguationData":[OSD([subQ0]),TDD([makeQuery(id+"F3.opExtrude","CAP_EDGE",EDGE,{"disambiguationData":[OSD([subQ0])],"isStart":false})])]})]}),makeQuery(id+"F7.opRevolve","SWEPT_FACE",FACE,{"disambiguationData":[OSD([subQ0])]})]}),makeQuery(id+"F3.boolean.opBoolean","MERGE",FACE,{"derivedFrom":[makeQuery(id+"F1.opExtrude","CAP_FACE",FACE,{"disambiguationData":[OSD([sQuery(id+"F0.wireOp",EDGE,"E0.bottom"),sQuery(id+"F0.wireOp",EDGE,"E0.top"),sQuery(id+"F0.wireOp",EDGE,"E0.right"),subQ1])],"isStart":true}),makeQuery(id+"F3.opExtrude","CAP_FACE",FACE,{"disambiguationData":[OSD([sQuery(id+"F0.wireOp",EDGE,"E1.bottom"),sQuery(id+"F0.wireOp",EDGE,"E1.top"),subQ1,subQ0])],"isStart":true})]})],"blendedInto":[makeQuery(id+"F3.boolean.opBoolean","MERGE",FACE,{"derivedFrom":[makeQuery(id+"F1.opExtrude","CAP_FACE",FACE,{"disambiguationData":[OSD([sQuery(id+"F0.wireOp",EDGE,"E0.bottom"),sQuery(id+"F0.wireOp",EDGE,"E0.top"),sQuery(id+"F0.wireOp",EDGE,"E0.right"),subQ1])],"isStart":true}),makeQuery(id+"F3.opExtrude","CAP_FACE",FACE,{"disambiguationData":[OSD([sQuery(id+"F0.wireOp",EDGE,"E1.bottom"),sQuery(id+"F0.wireOp",EDGE,"E1.top"),subQ1,subQ0])],"isStart":true})]})]});}
            fillet(context, id + "F14", {"entities" : qUnion([Q0, Q1]), "radius" : 5.08 * mm, "tangentPropagation" : true, "allowEdgeOverflow" : false});
        }
        {
            var Q0;
            Q0=makeQuery(id+"F6.opRevolve","SWEPT_FACE",FACE,{"disambiguationData":[OSD([sQuery(id+"F0.wireOp",EDGE,"E0.bottom"),sQuery(id+"F0.wireOp",EDGE,"E0.right")])]});
            var Q1;
            Q1=makeQuery(id+"F7.opRevolve","SWEPT_FACE",FACE,{"disambiguationData":[OSD([sQuery(id+"F0.wireOp",EDGE,"E1.top"),sQuery(id+"F0.wireOp",EDGE,"E1.right")])]});
            extrude(context, id + "F15", {"entities" : qUnion([Q0, Q1]), "operationType" : NewBodyOperationType.REMOVE, "oppositeDirection" : true, "depth" : 76.2 * mm, "offsetDistance" : 25.4 * mm});
        }
        {
            var Q0;
            {var subQ0=sQuery(id+"F0.wireOp",EDGE,"E0.right");var subQ1=sQuery(id+"F0.wireOp",EDGE,"E0.bottom");var subQ2=makeQuery(id+"F6.opRevolve","SWEPT_FACE",FACE,{"disambiguationData":[OSD([subQ1,subQ0])]});var subQ3=sQuery(id+"F0.wireOp",EDGE,"E1.right");var subQ4=sQuery(id+"F0.wireOp",EDGE,"E1.left");var subQ5=sQuery(id+"F0.wireOp",EDGE,"E1.top");var subQ6=sQuery(id+"F0.wireOp",EDGE,"E1.bottom");var subQ7=sQuery(id+"F0.wireOp",EDGE,"E0.top");Q0=makeQuery(id+"F15.boolean.opBoolean","COPY",EDGE,{"derivedFrom":makeQuery(id+"F15.opExtrude","SWEPT_EDGE",EDGE,{"disambiguationData":[OSD([subQ1,subQ7,subQ0,subQ6,subQ5,subQ4,subQ3]),TDD([makeQuery(id+"F8.opFillet","BLEND_VERTEX",VERTEX,{"blendedFrom":[makeQuery(id+"F6.boolean.opBoolean","INTERSECT",EDGE,{"derivedFrom":[makeQuery(id+"F5.boolean.opBoolean","MERGE",FACE,{"derivedFrom":[makeQuery(id+"F1.opExtrude","SWEPT_FACE",FACE,{"disambiguationData":[OSD([subQ0])]}),makeQuery(id+"F5.opExtrude","SWEPT_FACE",FACE,{"disambiguationData":[OSD([subQ0]),TDD([makeQuery(id+"F1.opExtrude","CAP_EDGE",EDGE,{"disambiguationData":[OSD([subQ0])],"isStart":false})])]})]}),subQ2]}),makeQuery(id+"F6.boolean.opBoolean","INTERSECT",EDGE,{"derivedFrom":[makeQuery(id+"F5.opExtrude","CAP_FACE",FACE,{"disambiguationData":[OSD([subQ1,subQ7,subQ0,subQ6,subQ5,subQ4,subQ3])],"isStart":false}),subQ2]}),subQ2],"blendedInto":[subQ2]})])]})});}
            var Q1;
            {var subQ0=sQuery(id+"F0.wireOp",EDGE,"E0.right");var subQ1=sQuery(id+"F0.wireOp",EDGE,"E0.bottom");var subQ2=makeQuery(id+"F6.opRevolve","SWEPT_FACE",FACE,{"disambiguationData":[OSD([subQ1,subQ0])]});var subQ3=sQuery(id+"F0.wireOp",EDGE,"E1.right");var subQ4=sQuery(id+"F0.wireOp",EDGE,"E1.left");var subQ5=sQuery(id+"F0.wireOp",EDGE,"E1.top");var subQ6=sQuery(id+"F0.wireOp",EDGE,"E1.bottom");var subQ7=sQuery(id+"F0.wireOp",EDGE,"E0.top");Q1=makeQuery(id+"F15.boolean.opBoolean","INTERSECT",EDGE,{"derivedFrom":[makeQuery(id+"F6.opRevolve","SWEPT_FACE",FACE,{"disambiguationData":[OSD([subQ7,subQ0])]}),makeQuery(id+"F15.opExtrude","SWEPT_FACE",FACE,{"disambiguationData":[OSD([subQ1,subQ7,subQ0,subQ6,subQ5,subQ4,subQ3]),TDD([makeQuery(id+"F8.opFillet","BLEND_EDGE",EDGE,{"blendedFrom":[makeQuery(id+"F6.boolean.opBoolean","INTERSECT",EDGE,{"derivedFrom":[makeQuery(id+"F5.opExtrude","CAP_FACE",FACE,{"disambiguationData":[OSD([subQ1,subQ7,subQ0,subQ6,subQ5,subQ4,subQ3])],"isStart":false}),subQ2]}),subQ2],"blendedInto":[subQ2]})])]})]});}
            var Q2;
            {var subQ0=sQuery(id+"F0.wireOp",EDGE,"E0.right");var subQ1=makeQuery(id+"F6.opRevolve","SWEPT_FACE",FACE,{"disambiguationData":[OSD([sQuery(id+"F0.wireOp",EDGE,"E0.top"),subQ0])]});Q2=makeQuery(id+"F8.opFillet","BLEND_EDGE",EDGE,{"blendedFrom":[makeQuery(id+"F6.boolean.opBoolean","INTERSECT",EDGE,{"derivedFrom":[makeQuery(id+"F5.boolean.opBoolean","MERGE",FACE,{"derivedFrom":[makeQuery(id+"F1.opExtrude","SWEPT_FACE",FACE,{"disambiguationData":[OSD([subQ0])]}),makeQuery(id+"F5.opExtrude","SWEPT_FACE",FACE,{"disambiguationData":[OSD([subQ0]),TDD([makeQuery(id+"F1.opExtrude","CAP_EDGE",EDGE,{"disambiguationData":[OSD([subQ0])],"isStart":false})])]})]}),subQ1]}),subQ1],"blendedInto":[subQ1]});}
            var Q3;
            {var subQ0=sQuery(id+"F0.wireOp",EDGE,"E0.right");var subQ1=sQuery(id+"F0.wireOp",EDGE,"E0.bottom");var subQ2=makeQuery(id+"F6.opRevolve","SWEPT_FACE",FACE,{"disambiguationData":[OSD([subQ1,subQ0])]});var subQ3=makeQuery(id+"F8.opFillet","BLEND_EDGE",EDGE,{"blendedFrom":[makeQuery(id+"F6.boolean.opBoolean","INTERSECT",EDGE,{"derivedFrom":[makeQuery(id+"F5.boolean.opBoolean","MERGE",FACE,{"derivedFrom":[makeQuery(id+"F1.opExtrude","SWEPT_FACE",FACE,{"disambiguationData":[OSD([subQ0])]}),makeQuery(id+"F5.opExtrude","SWEPT_FACE",FACE,{"disambiguationData":[OSD([subQ0]),TDD([makeQuery(id+"F1.opExtrude","CAP_EDGE",EDGE,{"disambiguationData":[OSD([subQ0])],"isStart":false})])]})]}),subQ2]}),subQ2],"blendedInto":[subQ2]});Q3=makeQuery(id+"F15.boolean.opBoolean","MERGE",EDGE,{"derivedFrom":[subQ3,makeQuery(id+"F15.opExtrude","CAP_EDGE",EDGE,{"disambiguationData":[OSD([subQ1,subQ0]),TDD([subQ3])],"isStart":true})]});}
            fillet(context, id + "F16", {"entities" : qUnion([Q0, Q1, Q2, Q3]), "radius" : 5.08 * mm, "tangentPropagation" : true, "allowEdgeOverflow" : false});
        }
    });
